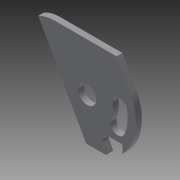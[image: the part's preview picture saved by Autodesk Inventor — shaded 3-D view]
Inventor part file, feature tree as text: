
AUTODESK INVENTOR PART (.ipt)
format: ipt  version: 2014 SP1 (Build 180222100, 222)  size: 116,224 bytes
history: native  units: in
note: dims shown in document units (in); Inventor stores cm internally (conversion verified against a paired STEP export)
features: extrude x1, sketch x1
ambient origin geometry x8: Origin, YZ Plane, XZ Plane, XY Plane, X Axis, Y Axis, Z Axis, Center Point
bodies: Solid1 (feature_tree)
feature tree (2):
  extrude  "Extrusion1"  Depth=0.0515in
  sketch  "Sketch1"  dims[d0=0.159in d1=0.348in d2=0.1285in d3=0.0725in d4=0.4275in d5=0.339in d6=0.1115in d7=0.4192in d8=0.073in d9=0.456in d10=0.18in d11=0.153in d12=0.0156in d13=0.17in d14=0.072in d15=0.05in d16=0.0479in d17=0.6185in d18=0.868in d19=0.545in d20=0.291in d21=0.0515in d22=0.0in]
